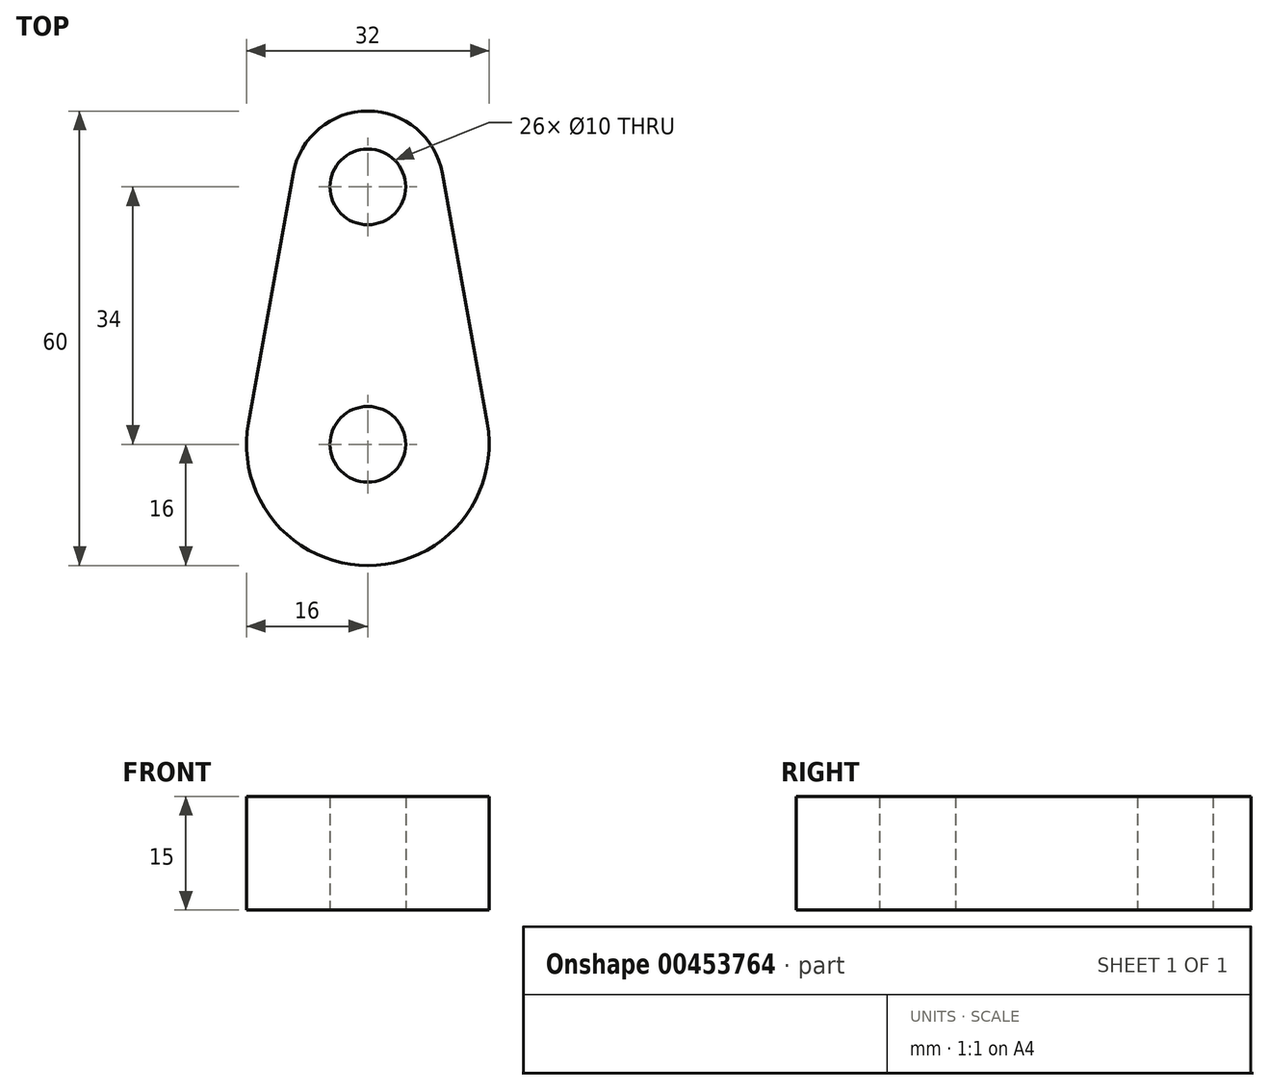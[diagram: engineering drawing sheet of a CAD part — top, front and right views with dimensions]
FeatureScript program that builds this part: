
annotation { "Feature Type Name" : "Feature", "Feature Type Description" : "" }
export const myFeature = defineFeature(function(context is Context, id is Id, definition is map)
    precondition{}
    {
        {
            var Q0;
            Q0=qCreatedBy(makeId("Top.planeOp"),FACE);
            var sketch = newSketch(context, id + "F0", { "sketchPlane" : qUnion([Q0])});
            skCircle(sketch, "E0", {"center": v(0, 0) * mm, "radius": 16 * mm});
            skCircle(sketch, "E1", {"center": v(0, 34) * mm, "radius": 10 * mm});
            skLineSegment(sketch, "E2", {"start": v(-9.84, 35.76) * mm, "end": v(-15.75, 2.82) * mm});
            skLineSegment(sketch, "E3", {"start": v(9.84, 35.76) * mm, "end": v(15.75, 2.82) * mm});
            skCircle(sketch, "E4", {"center": v(0, 34) * mm, "radius": 5 * mm});
            skCircle(sketch, "E5", {"center": v(0, 0) * mm, "radius": 5 * mm});
            skLineSegment(sketch, "E6", {"start": v(0, 61.17) * mm, "end": v(0, -20.6) * mm, "construction": true});
            skSolve(sketch);
        }
        {
            var Q0;
            {var subQ0=sQuery(id+"F0.wireOp",EDGE,"E2");Q0=makeQuery(id+"F0.imprint","IMPRINT",FACE,{"disambiguationData":[TD([[makeQuery(id+"F0.imprint","IMPRINT",EDGE,{"derivedFrom":subQ0}),1.0]])]});}
            var Q1;
            Q1=makeQuery(id+"F0.imprint","IMPRINT",FACE,{"disambiguationData":[TD([[makeQuery(id+"F0.imprint","IMPRINT",EDGE,{"derivedFrom":sQuery(id+"F0.wireOp",EDGE,"E4")}),-1.0]])]});
            var Q2;
            Q2=makeQuery(id+"F0.imprint","IMPRINT",FACE,{"disambiguationData":[TD([[makeQuery(id+"F0.imprint","IMPRINT",EDGE,{"derivedFrom":sQuery(id+"F0.wireOp",EDGE,"E5")}),-1.0]])]});
            extrude(context, id + "F1", {"entities" : qUnion([Q0, Q1, Q2]), "depth" : 15 * mm});
        }
    });
